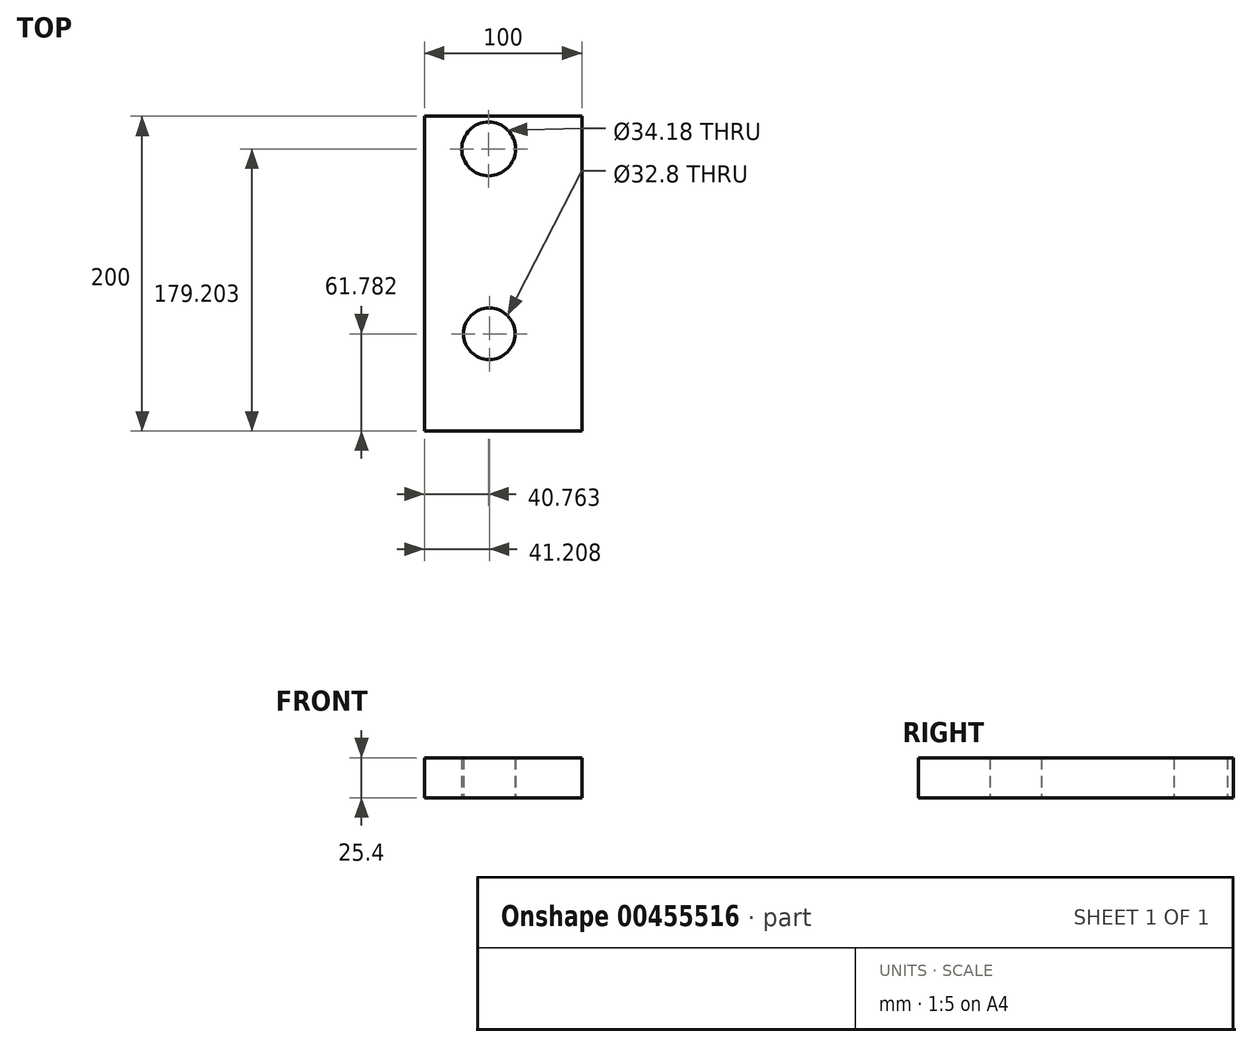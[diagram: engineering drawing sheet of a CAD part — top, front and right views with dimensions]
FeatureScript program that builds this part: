
annotation { "Feature Type Name" : "Feature", "Feature Type Description" : "" }
export const myFeature = defineFeature(function(context is Context, id is Id, definition is map)
    precondition{}
    {
        {
            var Q0;
            Q0=qCreatedBy(makeId("Top.planeOp"),FACE);
            var sketch = newSketch(context, id + "F0", { "sketchPlane" : qUnion([Q0])});
            skLineSegment(sketch, "E0.bottom", {"start": v(31.46, -23.94) * mm, "end": v(-68.54, -23.94) * mm});
            skLineSegment(sketch, "E0.top", {"start": v(31.46, 176.06) * mm, "end": v(-68.54, 176.06) * mm});
            skLineSegment(sketch, "E0.left", {"start": v(31.46, -23.94) * mm, "end": v(31.46, 176.06) * mm});
            skLineSegment(sketch, "E0.right", {"start": v(-68.54, -23.94) * mm, "end": v(-68.54, 176.06) * mm});
            skCircle(sketch, "E1", {"center": v(-27.78, 155.26) * mm, "radius": 17.09 * mm});
            skCircle(sketch, "E2", {"center": v(-27.33, 37.84) * mm, "radius": 16.4 * mm});
            skSolve(sketch);
        }
        {
            var Q0;
            Q0=makeQuery(id+"F0.imprint","IMPRINT",FACE,{"disambiguationData":[TD([[makeQuery(id+"F0.imprint","IMPRINT",EDGE,{"derivedFrom":sQuery(id+"F0.wireOp",EDGE,"E0.bottom")}),-1.0]])]});
            extrude(context, id + "F1", {"entities" : qUnion([Q0]), "depth" : 25.4 * mm, "offsetDistance" : 25.4 * mm});
        }
    });
